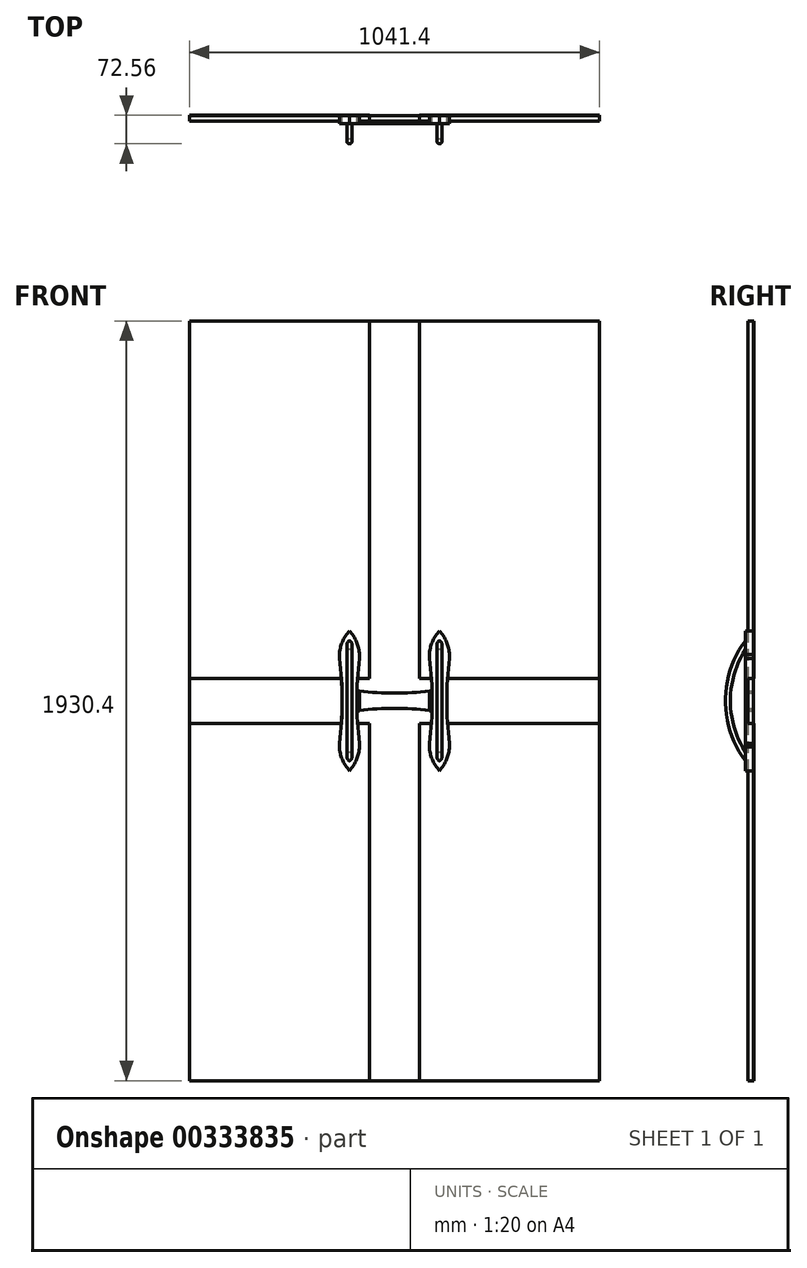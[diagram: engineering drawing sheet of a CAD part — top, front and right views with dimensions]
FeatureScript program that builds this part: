
annotation { "Feature Type Name" : "Feature", "Feature Type Description" : "" }
export const myFeature = defineFeature(function(context is Context, id is Id, definition is map)
    precondition{}
    {
        {
            var Q0;
            Q0=qCreatedBy(makeId("Front.planeOp"),FACE);
            var sketch = newSketch(context, id + "F0", { "sketchPlane" : qUnion([Q0])});
            skLineSegment(sketch, "E0.bottom", {"start": v(-936, -960.25) * mm, "end": v(105.4, -960.25) * mm});
            skLineSegment(sketch, "E0.top", {"start": v(-936, 970.15) * mm, "end": v(105.4, 970.15) * mm});
            skLineSegment(sketch, "E0.left", {"start": v(-936, -960.25) * mm, "end": v(-936, 970.15) * mm});
            skLineSegment(sketch, "E0.right", {"start": v(105.4, -960.25) * mm, "end": v(105.4, 970.15) * mm});
            skLineSegment(sketch, "E1", {"start": v(-478.8, 970.15) * mm, "end": v(-478.8, 62.1) * mm});
            skLineSegment(sketch, "E2", {"start": v(-478.8, 62.1) * mm, "end": v(-936, 62.1) * mm});
            skLineSegment(sketch, "E3", {"start": v(-351.8, 970.15) * mm, "end": v(-351.8, 62.1) * mm});
            skLineSegment(sketch, "E4", {"start": v(-351.8, 62.1) * mm, "end": v(105.4, 62.1) * mm});
            skLineSegment(sketch, "E5", {"start": v(105.4, -52.2) * mm, "end": v(-351.8, -52.2) * mm});
            skLineSegment(sketch, "E6", {"start": v(-351.8, -52.2) * mm, "end": v(-351.8, -960.25) * mm});
            skLineSegment(sketch, "E7", {"start": v(-936, -52.2) * mm, "end": v(-478.8, -52.2) * mm});
            skLineSegment(sketch, "E8", {"start": v(-478.8, -52.2) * mm, "end": v(-478.8, -960.25) * mm});
            skLineSegment(sketch, "E9", {"start": v(-415.3, 970.15) * mm, "end": v(-415.3, -960.25) * mm});
            skLineSegment(sketch, "E10.bottom", {"start": v(-555, 182.75) * mm, "end": v(-504.2, 182.75) * mm});
            skLineSegment(sketch, "E10.top", {"start": v(-555, -172.85) * mm, "end": v(-504.2, -172.85) * mm});
            skLineSegment(sketch, "E10.left", {"start": v(-555, 182.75) * mm, "end": v(-555, -172.85) * mm});
            skLineSegment(sketch, "E10.right", {"start": v(-504.2, 182.75) * mm, "end": v(-504.2, -172.85) * mm});
            skLineSegment(sketch, "E11.bottom", {"start": v(-326.4, 182.75) * mm, "end": v(-275.6, 182.75) * mm});
            skLineSegment(sketch, "E11.top", {"start": v(-326.4, -172.85) * mm, "end": v(-275.6, -172.85) * mm});
            skLineSegment(sketch, "E11.left", {"start": v(-326.4, 182.75) * mm, "end": v(-326.4, -172.85) * mm});
            skLineSegment(sketch, "E11.right", {"start": v(-275.6, 182.75) * mm, "end": v(-275.6, -172.85) * mm});
            skLineSegment(sketch, "E12.bottom", {"start": v(-510.66, 30.35) * mm, "end": v(-319.94, 30.35) * mm});
            skLineSegment(sketch, "E12.top", {"start": v(-510.66, -20.45) * mm, "end": v(-319.94, -20.45) * mm});
            skLineSegment(sketch, "E12.left", {"start": v(-504.2, 30.35) * mm, "end": v(-504.2, -20.45) * mm});
            skLineSegment(sketch, "E12.right", {"start": v(-326.4, 30.35) * mm, "end": v(-326.4, -20.45) * mm});
            skArc(sketch, "E13", {"start": v(-555, -103.11) * mm, "mid": v(-549.29, -140.52) * mm, "end": v(-529.6, -172.85) * mm});
            skLineSegment(sketch, "E14", {"start": v(-936, 4.95) * mm, "end": v(105.4, 4.95) * mm});
            skArc(sketch, "E15.MirrorCS", {"start": v(-555, 113.02) * mm, "mid": v(-549.29, 150.43) * mm, "end": v(-529.6, 182.75) * mm});
            skArc(sketch, "E16.MirrorCS", {"start": v(-275.6, -103.11) * mm, "mid": v(-281.31, -140.52) * mm, "end": v(-301, -172.85) * mm});
            skArc(sketch, "E17.MirrorCS", {"start": v(-275.6, 113.02) * mm, "mid": v(-281.31, 150.43) * mm, "end": v(-301, 182.75) * mm});
            skLineSegment(sketch, "E18", {"start": v(-529.6, -172.85) * mm, "end": v(-529.6, -92.29) * mm});
            skArc(sketch, "E19.MirrorCS", {"start": v(-504.2, -103.11) * mm, "mid": v(-509.91, -140.52) * mm, "end": v(-529.6, -172.85) * mm});
            skArc(sketch, "E20.MirrorCS", {"start": v(-504.2, 113.02) * mm, "mid": v(-509.91, 150.43) * mm, "end": v(-529.6, 182.75) * mm});
            skArc(sketch, "E21.MirrorCS", {"start": v(-326.4, 113.02) * mm, "mid": v(-320.69, 150.43) * mm, "end": v(-301, 182.75) * mm});
            skArc(sketch, "E22.MirrorCS", {"start": v(-326.4, -103.11) * mm, "mid": v(-320.69, -140.52) * mm, "end": v(-301, -172.85) * mm});
            skArc(sketch, "E23", {"start": v(-555, -103.11) * mm, "mid": v(-548.16, 4.95) * mm, "end": v(-555, 113.02) * mm});
            skArc(sketch, "E24.MirrorCS", {"start": v(-504.2, -103.11) * mm, "mid": v(-511.03, 4.95) * mm, "end": v(-504.2, 113.02) * mm});
            skArc(sketch, "E25.MirrorCS", {"start": v(-275.6, -103.11) * mm, "mid": v(-282.43, 4.95) * mm, "end": v(-275.6, 113.02) * mm});
            skArc(sketch, "E26.MirrorCS", {"start": v(-326.4, -103.11) * mm, "mid": v(-319.56, 4.95) * mm, "end": v(-326.4, 113.02) * mm});
            skArc(sketch, "E27", {"start": v(-319.94, -20.45) * mm, "mid": v(-415.3, -14.24) * mm, "end": v(-510.66, -20.45) * mm});
            skArc(sketch, "E28.MirrorCS", {"start": v(-319.94, 30.35) * mm, "mid": v(-415.3, 24.14) * mm, "end": v(-510.66, 30.35) * mm});
            skSolve(sketch);
        }
        {
            var Q0;
            {var subQ9=sQuery(id+"F0.wireOp",EDGE,"E3");Q0=makeQuery(id+"F0.imprint","IMPRINT",FACE,{"disambiguationData":[TD([[makeQuery(id+"F0.imprint","IMPRINT",EDGE,{"derivedFrom":subQ9}),-1.0]])]});}
            var Q1;
            {var subQ1=sQuery(id+"F0.wireOp",EDGE,"E1");Q1=makeQuery(id+"F0.imprint","IMPRINT",FACE,{"disambiguationData":[TD([[makeQuery(id+"F0.imprint","IMPRINT",EDGE,{"derivedFrom":subQ1}),1.0]])]});}
            var Q2;
            {var subQ0=sQuery(id+"F0.wireOp",EDGE,"E4");var subQ1=sQuery(id+"F0.wireOp",EDGE,"E0.right");var subQ2=makeQuery(id+"F0.imprint","INTERSECT",VERTEX,{"derivedFrom":[subQ1,subQ0]});Q2=makeQuery(id+"F0.imprint","IMPRINT",FACE,{"disambiguationData":[TD([[makeQuery(id+"F0.imprint","IMPRINT",EDGE,{"disambiguationData":[TD([[subQ2,1.0]])],"derivedFrom":subQ1}),1.0]])]});}
            var Q3;
            {var subQ0=sQuery(id+"F0.wireOp",EDGE,"E5");var subQ1=sQuery(id+"F0.wireOp",EDGE,"E0.right");var subQ2=makeQuery(id+"F0.imprint","INTERSECT",VERTEX,{"derivedFrom":[subQ1,subQ0]});Q3=makeQuery(id+"F0.imprint","IMPRINT",FACE,{"disambiguationData":[TD([[makeQuery(id+"F0.imprint","IMPRINT",EDGE,{"disambiguationData":[TD([[subQ2,-1.0]])],"derivedFrom":subQ1}),1.0]])]});}
            var Q4;
            {var subQ5=sQuery(id+"F0.wireOp",EDGE,"E6");Q4=makeQuery(id+"F0.imprint","IMPRINT",FACE,{"disambiguationData":[TD([[makeQuery(id+"F0.imprint","IMPRINT",EDGE,{"derivedFrom":subQ5}),-1.0]])]});}
            var Q5;
            {var subQ5=sQuery(id+"F0.wireOp",EDGE,"E8");Q5=makeQuery(id+"F0.imprint","IMPRINT",FACE,{"disambiguationData":[TD([[makeQuery(id+"F0.imprint","IMPRINT",EDGE,{"derivedFrom":subQ5}),1.0]])]});}
            var Q6;
            {var subQ0=sQuery(id+"F0.wireOp",EDGE,"E7");var subQ1=sQuery(id+"F0.wireOp",EDGE,"E0.left");var subQ2=makeQuery(id+"F0.imprint","INTERSECT",VERTEX,{"derivedFrom":[subQ1,subQ0]});Q6=makeQuery(id+"F0.imprint","IMPRINT",FACE,{"disambiguationData":[TD([[makeQuery(id+"F0.imprint","IMPRINT",EDGE,{"disambiguationData":[TD([[subQ2,-1.0]])],"derivedFrom":subQ1}),-1.0]])]});}
            var Q7;
            {var subQ0=sQuery(id+"F0.wireOp",EDGE,"E2");var subQ1=sQuery(id+"F0.wireOp",EDGE,"E0.left");var subQ2=makeQuery(id+"F0.imprint","INTERSECT",VERTEX,{"derivedFrom":[subQ1,subQ0]});Q7=makeQuery(id+"F0.imprint","IMPRINT",FACE,{"disambiguationData":[TD([[makeQuery(id+"F0.imprint","IMPRINT",EDGE,{"disambiguationData":[TD([[subQ2,1.0]])],"derivedFrom":subQ1}),-1.0]])]});}
            var Q8;
            {var subQ0=sQuery(id+"F0.wireOp",EDGE,"E24.MirrorCS");var subQ1=sQuery(id+"F0.wireOp",EDGE,"E7");var subQ2=makeQuery(id+"F0.imprint","INTERSECT",VERTEX,{"derivedFrom":[subQ1,subQ0]});Q8=makeQuery(id+"F0.imprint","IMPRINT",FACE,{"disambiguationData":[TD([[makeQuery(id+"F0.imprint","IMPRINT",EDGE,{"disambiguationData":[TD([[subQ2,-1.0]])],"derivedFrom":subQ1}),1.0]])]});}
            var Q9;
            {var subQ0=sQuery(id+"F0.wireOp",EDGE,"E10.left");var subQ1=sQuery(id+"F0.wireOp",EDGE,"E7");var subQ2=makeQuery(id+"F0.imprint","INTERSECT",VERTEX,{"derivedFrom":[subQ1,subQ0]});Q9=makeQuery(id+"F0.imprint","IMPRINT",FACE,{"disambiguationData":[TD([[makeQuery(id+"F0.imprint","IMPRINT",EDGE,{"disambiguationData":[TD([[subQ2,-1.0]])],"derivedFrom":subQ1}),1.0]])]});}
            var Q10;
            {var subQ0=sQuery(id+"F0.wireOp",EDGE,"E23");var subQ1=sQuery(id+"F0.wireOp",EDGE,"E2");var subQ2=makeQuery(id+"F0.imprint","INTERSECT",VERTEX,{"derivedFrom":[subQ1,subQ0]});Q10=makeQuery(id+"F0.imprint","IMPRINT",FACE,{"disambiguationData":[TD([[makeQuery(id+"F0.imprint","IMPRINT",EDGE,{"disambiguationData":[TD([[subQ2,-1.0]])],"derivedFrom":subQ1}),1.0]])]});}
            var Q11;
            {var subQ0=sQuery(id+"F0.wireOp",EDGE,"E10.right");var subQ1=sQuery(id+"F0.wireOp",EDGE,"E2");var subQ2=makeQuery(id+"F0.imprint","INTERSECT",VERTEX,{"derivedFrom":[subQ1,subQ0]});Q11=makeQuery(id+"F0.imprint","IMPRINT",FACE,{"disambiguationData":[TD([[makeQuery(id+"F0.imprint","IMPRINT",EDGE,{"disambiguationData":[TD([[subQ2,-1.0]])],"derivedFrom":subQ1}),1.0]])]});}
            var Q12;
            {var subQ0=sQuery(id+"F0.wireOp",EDGE,"E11.left");var subQ1=sQuery(id+"F0.wireOp",EDGE,"E4");var subQ2=makeQuery(id+"F0.imprint","INTERSECT",VERTEX,{"derivedFrom":[subQ1,subQ0]});Q12=makeQuery(id+"F0.imprint","IMPRINT",FACE,{"disambiguationData":[TD([[makeQuery(id+"F0.imprint","IMPRINT",EDGE,{"disambiguationData":[TD([[subQ2,-1.0]])],"derivedFrom":subQ1}),-1.0]])]});}
            var Q13;
            {var subQ0=sQuery(id+"F0.wireOp",EDGE,"E26.MirrorCS");var subQ1=sQuery(id+"F0.wireOp",EDGE,"E5");var subQ2=makeQuery(id+"F0.imprint","INTERSECT",VERTEX,{"derivedFrom":[subQ1,subQ0]});Q13=makeQuery(id+"F0.imprint","IMPRINT",FACE,{"disambiguationData":[TD([[makeQuery(id+"F0.imprint","IMPRINT",EDGE,{"disambiguationData":[TD([[subQ2,-1.0]])],"derivedFrom":subQ1}),-1.0]])]});}
            var Q14;
            {var subQ0=sQuery(id+"F0.wireOp",EDGE,"E27");var subQ1=sQuery(id+"F0.wireOp",EDGE,"E9");var subQ2=makeQuery(id+"F0.imprint","INTERSECT",VERTEX,{"derivedFrom":[subQ1,subQ0]});Q14=makeQuery(id+"F0.imprint","IMPRINT",FACE,{"disambiguationData":[TD([[makeQuery(id+"F0.imprint","IMPRINT",EDGE,{"disambiguationData":[TD([[subQ2,-1.0]])],"derivedFrom":subQ1}),1.0]])]});}
            var Q15;
            {var subQ0=sQuery(id+"F0.wireOp",EDGE,"E27");var subQ1=sQuery(id+"F0.wireOp",EDGE,"E9");var subQ2=makeQuery(id+"F0.imprint","INTERSECT",VERTEX,{"derivedFrom":[subQ1,subQ0]});Q15=makeQuery(id+"F0.imprint","IMPRINT",FACE,{"disambiguationData":[TD([[makeQuery(id+"F0.imprint","IMPRINT",EDGE,{"disambiguationData":[TD([[subQ2,-1.0]])],"derivedFrom":subQ1}),-1.0]])]});}
            var Q16;
            {var subQ0=sQuery(id+"F0.wireOp",EDGE,"E12.bottom");var subQ1=sQuery(id+"F0.wireOp",EDGE,"E9");var subQ2=makeQuery(id+"F0.imprint","INTERSECT",VERTEX,{"derivedFrom":[subQ1,subQ0]});Q16=makeQuery(id+"F0.imprint","IMPRINT",FACE,{"disambiguationData":[TD([[makeQuery(id+"F0.imprint","IMPRINT",EDGE,{"disambiguationData":[TD([[subQ2,-1.0]])],"derivedFrom":subQ1}),-1.0]])]});}
            var Q17;
            {var subQ0=sQuery(id+"F0.wireOp",EDGE,"E12.bottom");var subQ1=sQuery(id+"F0.wireOp",EDGE,"E9");var subQ2=makeQuery(id+"F0.imprint","INTERSECT",VERTEX,{"derivedFrom":[subQ1,subQ0]});Q17=makeQuery(id+"F0.imprint","IMPRINT",FACE,{"disambiguationData":[TD([[makeQuery(id+"F0.imprint","IMPRINT",EDGE,{"disambiguationData":[TD([[subQ2,-1.0]])],"derivedFrom":subQ1}),1.0]])]});}
            var Q18;
            {var subQ0=sQuery(id+"F0.wireOp",EDGE,"E11.right");var subQ1=sQuery(id+"F0.wireOp",EDGE,"E5");var subQ2=makeQuery(id+"F0.imprint","INTERSECT",VERTEX,{"derivedFrom":[subQ1,subQ0]});Q18=makeQuery(id+"F0.imprint","IMPRINT",FACE,{"disambiguationData":[TD([[makeQuery(id+"F0.imprint","IMPRINT",EDGE,{"disambiguationData":[TD([[subQ2,-1.0]])],"derivedFrom":subQ1}),-1.0]])]});}
            var Q19;
            {var subQ0=sQuery(id+"F0.wireOp",EDGE,"E25.MirrorCS");var subQ1=sQuery(id+"F0.wireOp",EDGE,"E4");var subQ2=makeQuery(id+"F0.imprint","INTERSECT",VERTEX,{"derivedFrom":[subQ1,subQ0]});Q19=makeQuery(id+"F0.imprint","IMPRINT",FACE,{"disambiguationData":[TD([[makeQuery(id+"F0.imprint","IMPRINT",EDGE,{"disambiguationData":[TD([[subQ2,-1.0]])],"derivedFrom":subQ1}),-1.0]])]});}
            extrude(context, id + "F1", {"entities" : qUnion([Q0, Q1, Q2, Q3, Q4, Q5, Q6, Q7, Q8, Q9, Q10, Q11, Q12, Q13, Q14, Q15, Q16, Q17, Q18, Q19]), "depth" : 14.29 * mm});
        }
        {
            var Q0;
            {var subQ14=sQuery(id+"F0.wireOp",EDGE,"E3");Q0=makeQuery(id+"F0.imprint","IMPRINT",FACE,{"disambiguationData":[TD([[makeQuery(id+"F0.imprint","IMPRINT",EDGE,{"derivedFrom":subQ14}),1.0]])]});}
            var Q1;
            {var subQ16=sQuery(id+"F0.wireOp",EDGE,"E1");Q1=makeQuery(id+"F0.imprint","IMPRINT",FACE,{"disambiguationData":[TD([[makeQuery(id+"F0.imprint","IMPRINT",EDGE,{"derivedFrom":subQ16}),-1.0]])]});}
            var Q2;
            {var subQ11=sQuery(id+"F0.wireOp",EDGE,"E8");Q2=makeQuery(id+"F0.imprint","IMPRINT",FACE,{"disambiguationData":[TD([[makeQuery(id+"F0.imprint","IMPRINT",EDGE,{"derivedFrom":subQ11}),-1.0]])]});}
            var Q3;
            {var subQ10=sQuery(id+"F0.wireOp",EDGE,"E6");Q3=makeQuery(id+"F0.imprint","IMPRINT",FACE,{"disambiguationData":[TD([[makeQuery(id+"F0.imprint","IMPRINT",EDGE,{"derivedFrom":subQ10}),1.0]])]});}
            var Q4;
            {var subQ0=sQuery(id+"F0.wireOp",EDGE,"E11.right");var subQ1=sQuery(id+"F0.wireOp",EDGE,"E11.bottom");var subQ2=makeQuery(id+"F0.imprint","INTERSECT",VERTEX,{"derivedFrom":[subQ1,subQ0]});Q4=makeQuery(id+"F0.imprint","IMPRINT",FACE,{"disambiguationData":[TD([[makeQuery(id+"F0.imprint","IMPRINT",EDGE,{"disambiguationData":[TD([[subQ2,-1.0]])],"derivedFrom":subQ0}),-1.0]])]});}
            var Q5;
            {var subQ0=sQuery(id+"F0.wireOp",EDGE,"E11.left");var subQ1=sQuery(id+"F0.wireOp",EDGE,"E11.bottom");var subQ2=makeQuery(id+"F0.imprint","INTERSECT",VERTEX,{"derivedFrom":[subQ1,subQ0]});Q5=makeQuery(id+"F0.imprint","IMPRINT",FACE,{"disambiguationData":[TD([[makeQuery(id+"F0.imprint","IMPRINT",EDGE,{"disambiguationData":[TD([[subQ2,-1.0]])],"derivedFrom":subQ0}),1.0]])]});}
            var Q6;
            {var subQ0=sQuery(id+"F0.wireOp",EDGE,"E10.right");var subQ1=sQuery(id+"F0.wireOp",EDGE,"E10.bottom");var subQ2=makeQuery(id+"F0.imprint","INTERSECT",VERTEX,{"derivedFrom":[subQ1,subQ0]});Q6=makeQuery(id+"F0.imprint","IMPRINT",FACE,{"disambiguationData":[TD([[makeQuery(id+"F0.imprint","IMPRINT",EDGE,{"disambiguationData":[TD([[subQ2,-1.0]])],"derivedFrom":subQ0}),-1.0]])]});}
            var Q7;
            {var subQ0=sQuery(id+"F0.wireOp",EDGE,"E10.left");var subQ1=sQuery(id+"F0.wireOp",EDGE,"E10.bottom");var subQ2=makeQuery(id+"F0.imprint","INTERSECT",VERTEX,{"derivedFrom":[subQ1,subQ0]});Q7=makeQuery(id+"F0.imprint","IMPRINT",FACE,{"disambiguationData":[TD([[makeQuery(id+"F0.imprint","IMPRINT",EDGE,{"disambiguationData":[TD([[subQ2,-1.0]])],"derivedFrom":subQ0}),1.0]])]});}
            var Q8;
            {var subQ0=sQuery(id+"F0.wireOp",EDGE,"E10.left");var subQ1=sQuery(id+"F0.wireOp",EDGE,"E10.top");var subQ2=makeQuery(id+"F0.imprint","INTERSECT",VERTEX,{"derivedFrom":[subQ1,subQ0]});Q8=makeQuery(id+"F0.imprint","IMPRINT",FACE,{"disambiguationData":[TD([[makeQuery(id+"F0.imprint","IMPRINT",EDGE,{"disambiguationData":[TD([[subQ2,1.0]])],"derivedFrom":subQ0}),1.0]])]});}
            var Q9;
            {var subQ0=sQuery(id+"F0.wireOp",EDGE,"E10.right");var subQ1=sQuery(id+"F0.wireOp",EDGE,"E10.top");var subQ2=makeQuery(id+"F0.imprint","INTERSECT",VERTEX,{"derivedFrom":[subQ1,subQ0]});Q9=makeQuery(id+"F0.imprint","IMPRINT",FACE,{"disambiguationData":[TD([[makeQuery(id+"F0.imprint","IMPRINT",EDGE,{"disambiguationData":[TD([[subQ2,1.0]])],"derivedFrom":subQ0}),-1.0]])]});}
            var Q10;
            {var subQ0=sQuery(id+"F0.wireOp",EDGE,"E11.left");var subQ1=sQuery(id+"F0.wireOp",EDGE,"E11.top");var subQ2=makeQuery(id+"F0.imprint","INTERSECT",VERTEX,{"derivedFrom":[subQ1,subQ0]});Q10=makeQuery(id+"F0.imprint","IMPRINT",FACE,{"disambiguationData":[TD([[makeQuery(id+"F0.imprint","IMPRINT",EDGE,{"disambiguationData":[TD([[subQ2,1.0]])],"derivedFrom":subQ0}),1.0]])]});}
            var Q11;
            {var subQ0=sQuery(id+"F0.wireOp",EDGE,"E11.right");var subQ1=sQuery(id+"F0.wireOp",EDGE,"E11.top");var subQ2=makeQuery(id+"F0.imprint","INTERSECT",VERTEX,{"derivedFrom":[subQ1,subQ0]});Q11=makeQuery(id+"F0.imprint","IMPRINT",FACE,{"disambiguationData":[TD([[makeQuery(id+"F0.imprint","IMPRINT",EDGE,{"disambiguationData":[TD([[subQ2,1.0]])],"derivedFrom":subQ0}),-1.0]])]});}
            var Q12;
            {var subQ0=sQuery(id+"F0.wireOp",EDGE,"E23");var subQ1=sQuery(id+"F0.wireOp",EDGE,"E2");var subQ2=makeQuery(id+"F0.imprint","INTERSECT",VERTEX,{"derivedFrom":[subQ1,subQ0]});Q12=makeQuery(id+"F0.imprint","IMPRINT",FACE,{"disambiguationData":[TD([[makeQuery(id+"F0.imprint","IMPRINT",EDGE,{"disambiguationData":[TD([[subQ2,-1.0]])],"derivedFrom":subQ1}),-1.0]])]});}
            var Q13;
            {var subQ0=sQuery(id+"F0.wireOp",EDGE,"E10.right");var subQ1=sQuery(id+"F0.wireOp",EDGE,"E2");var subQ2=makeQuery(id+"F0.imprint","INTERSECT",VERTEX,{"derivedFrom":[subQ1,subQ0]});Q13=makeQuery(id+"F0.imprint","IMPRINT",FACE,{"disambiguationData":[TD([[makeQuery(id+"F0.imprint","IMPRINT",EDGE,{"disambiguationData":[TD([[subQ2,-1.0]])],"derivedFrom":subQ1}),-1.0]])]});}
            var Q14;
            {var subQ0=sQuery(id+"F0.wireOp",EDGE,"E24.MirrorCS");var subQ1=sQuery(id+"F0.wireOp",EDGE,"E7");var subQ2=makeQuery(id+"F0.imprint","INTERSECT",VERTEX,{"derivedFrom":[subQ1,subQ0]});Q14=makeQuery(id+"F0.imprint","IMPRINT",FACE,{"disambiguationData":[TD([[makeQuery(id+"F0.imprint","IMPRINT",EDGE,{"disambiguationData":[TD([[subQ2,-1.0]])],"derivedFrom":subQ1}),-1.0]])]});}
            var Q15;
            {var subQ0=sQuery(id+"F0.wireOp",EDGE,"E10.left");var subQ1=sQuery(id+"F0.wireOp",EDGE,"E7");var subQ2=makeQuery(id+"F0.imprint","INTERSECT",VERTEX,{"derivedFrom":[subQ1,subQ0]});Q15=makeQuery(id+"F0.imprint","IMPRINT",FACE,{"disambiguationData":[TD([[makeQuery(id+"F0.imprint","IMPRINT",EDGE,{"disambiguationData":[TD([[subQ2,-1.0]])],"derivedFrom":subQ1}),-1.0]])]});}
            var Q16;
            {var subQ0=sQuery(id+"F0.wireOp",EDGE,"E11.right");var subQ1=sQuery(id+"F0.wireOp",EDGE,"E5");var subQ2=makeQuery(id+"F0.imprint","INTERSECT",VERTEX,{"derivedFrom":[subQ1,subQ0]});Q16=makeQuery(id+"F0.imprint","IMPRINT",FACE,{"disambiguationData":[TD([[makeQuery(id+"F0.imprint","IMPRINT",EDGE,{"disambiguationData":[TD([[subQ2,-1.0]])],"derivedFrom":subQ1}),1.0]])]});}
            var Q17;
            {var subQ0=sQuery(id+"F0.wireOp",EDGE,"E26.MirrorCS");var subQ1=sQuery(id+"F0.wireOp",EDGE,"E5");var subQ2=makeQuery(id+"F0.imprint","INTERSECT",VERTEX,{"derivedFrom":[subQ1,subQ0]});Q17=makeQuery(id+"F0.imprint","IMPRINT",FACE,{"disambiguationData":[TD([[makeQuery(id+"F0.imprint","IMPRINT",EDGE,{"disambiguationData":[TD([[subQ2,-1.0]])],"derivedFrom":subQ1}),1.0]])]});}
            var Q18;
            {var subQ0=sQuery(id+"F0.wireOp",EDGE,"E11.left");var subQ1=sQuery(id+"F0.wireOp",EDGE,"E4");var subQ2=makeQuery(id+"F0.imprint","INTERSECT",VERTEX,{"derivedFrom":[subQ1,subQ0]});Q18=makeQuery(id+"F0.imprint","IMPRINT",FACE,{"disambiguationData":[TD([[makeQuery(id+"F0.imprint","IMPRINT",EDGE,{"disambiguationData":[TD([[subQ2,-1.0]])],"derivedFrom":subQ1}),1.0]])]});}
            var Q19;
            {var subQ0=sQuery(id+"F0.wireOp",EDGE,"E25.MirrorCS");var subQ1=sQuery(id+"F0.wireOp",EDGE,"E4");var subQ2=makeQuery(id+"F0.imprint","INTERSECT",VERTEX,{"derivedFrom":[subQ1,subQ0]});Q19=makeQuery(id+"F0.imprint","IMPRINT",FACE,{"disambiguationData":[TD([[makeQuery(id+"F0.imprint","IMPRINT",EDGE,{"disambiguationData":[TD([[subQ2,-1.0]])],"derivedFrom":subQ1}),1.0]])]});}
            extrude(context, id + "F2", {"entities" : qUnion([Q0, Q1, Q2, Q3, Q4, Q5, Q6, Q7, Q8, Q9, Q10, Q11, Q12, Q13, Q14, Q15, Q16, Q17, Q18, Q19]), "oppositeDirection" : true, "depth" : ((1 + 11 / 16) - 9 / 16) * mm});
        }
        {
            var Q0;
            {var subQ5=sQuery(id+"F0.wireOp",EDGE,"E24.MirrorCS");var subQ8=sQuery(id+"F0.wireOp",EDGE,"E2");var subQ9=makeQuery(id+"F0.imprint","INTERSECT",VERTEX,{"derivedFrom":[subQ8,subQ5]});Q0=makeQuery(id+"F0.imprint","IMPRINT",FACE,{"disambiguationData":[TD([[makeQuery(id+"F0.imprint","IMPRINT",EDGE,{"disambiguationData":[TD([[subQ9,-1.0]])],"derivedFrom":subQ8}),-1.0]])]});}
            var Q1;
            {var subQ0=sQuery(id+"F0.wireOp",EDGE,"E24.MirrorCS");var subQ5=sQuery(id+"F0.wireOp",EDGE,"E2");var subQ8=makeQuery(id+"F0.imprint","INTERSECT",VERTEX,{"derivedFrom":[subQ5,subQ0]});Q1=makeQuery(id+"F0.imprint","IMPRINT",FACE,{"disambiguationData":[TD([[makeQuery(id+"F0.imprint","IMPRINT",EDGE,{"disambiguationData":[TD([[subQ8,-1.0]])],"derivedFrom":subQ5}),1.0]])]});}
            var Q2;
            {var subQ2=sQuery(id+"F0.wireOp",EDGE,"E7");var subQ4=sQuery(id+"F0.wireOp",EDGE,"E23");var subQ5=makeQuery(id+"F0.imprint","INTERSECT",VERTEX,{"derivedFrom":[subQ2,subQ4]});Q2=makeQuery(id+"F0.imprint","IMPRINT",FACE,{"disambiguationData":[TD([[makeQuery(id+"F0.imprint","IMPRINT",EDGE,{"disambiguationData":[TD([[subQ5,-1.0]])],"derivedFrom":subQ2}),1.0]])]});}
            var Q3;
            {var subQ9=sQuery(id+"F0.wireOp",EDGE,"E23");var subQ11=sQuery(id+"F0.wireOp",EDGE,"E7");var subQ12=makeQuery(id+"F0.imprint","INTERSECT",VERTEX,{"derivedFrom":[subQ11,subQ9]});Q3=makeQuery(id+"F0.imprint","IMPRINT",FACE,{"disambiguationData":[TD([[makeQuery(id+"F0.imprint","IMPRINT",EDGE,{"disambiguationData":[TD([[subQ12,-1.0]])],"derivedFrom":subQ11}),-1.0]])]});}
            var Q4;
            {var subQ0=sQuery(id+"F0.wireOp",EDGE,"E14");var subQ1=sQuery(id+"F0.wireOp",EDGE,"E9");var subQ2=makeQuery(id+"F0.imprint","INTERSECT",VERTEX,{"derivedFrom":[subQ1,subQ0]});Q4=makeQuery(id+"F0.imprint","IMPRINT",FACE,{"disambiguationData":[TD([[makeQuery(id+"F0.imprint","IMPRINT",EDGE,{"disambiguationData":[TD([[subQ2,-1.0]])],"derivedFrom":subQ1}),-1.0]])]});}
            var Q5;
            {var subQ0=sQuery(id+"F0.wireOp",EDGE,"E28.MirrorCS");var subQ1=sQuery(id+"F0.wireOp",EDGE,"E9");var subQ2=makeQuery(id+"F0.imprint","INTERSECT",VERTEX,{"derivedFrom":[subQ1,subQ0]});Q5=makeQuery(id+"F0.imprint","IMPRINT",FACE,{"disambiguationData":[TD([[makeQuery(id+"F0.imprint","IMPRINT",EDGE,{"disambiguationData":[TD([[subQ2,-1.0]])],"derivedFrom":subQ1}),-1.0]])]});}
            var Q6;
            {var subQ0=sQuery(id+"F0.wireOp",EDGE,"E28.MirrorCS");var subQ1=sQuery(id+"F0.wireOp",EDGE,"E9");var subQ2=makeQuery(id+"F0.imprint","INTERSECT",VERTEX,{"derivedFrom":[subQ1,subQ0]});Q6=makeQuery(id+"F0.imprint","IMPRINT",FACE,{"disambiguationData":[TD([[makeQuery(id+"F0.imprint","IMPRINT",EDGE,{"disambiguationData":[TD([[subQ2,-1.0]])],"derivedFrom":subQ1}),1.0]])]});}
            var Q7;
            {var subQ0=sQuery(id+"F0.wireOp",EDGE,"E14");var subQ1=sQuery(id+"F0.wireOp",EDGE,"E9");var subQ2=makeQuery(id+"F0.imprint","INTERSECT",VERTEX,{"derivedFrom":[subQ1,subQ0]});Q7=makeQuery(id+"F0.imprint","IMPRINT",FACE,{"disambiguationData":[TD([[makeQuery(id+"F0.imprint","IMPRINT",EDGE,{"disambiguationData":[TD([[subQ2,-1.0]])],"derivedFrom":subQ1}),1.0]])]});}
            var Q8;
            {var subQ2=sQuery(id+"F0.wireOp",EDGE,"E5");var subQ4=sQuery(id+"F0.wireOp",EDGE,"E25.MirrorCS");var subQ5=makeQuery(id+"F0.imprint","INTERSECT",VERTEX,{"derivedFrom":[subQ2,subQ4]});Q8=makeQuery(id+"F0.imprint","IMPRINT",FACE,{"disambiguationData":[TD([[makeQuery(id+"F0.imprint","IMPRINT",EDGE,{"disambiguationData":[TD([[subQ5,-1.0]])],"derivedFrom":subQ2}),-1.0]])]});}
            var Q9;
            {var subQ0=sQuery(id+"F0.wireOp",EDGE,"E26.MirrorCS");var subQ6=sQuery(id+"F0.wireOp",EDGE,"E4");var subQ8=makeQuery(id+"F0.imprint","INTERSECT",VERTEX,{"derivedFrom":[subQ6,subQ0]});Q9=makeQuery(id+"F0.imprint","IMPRINT",FACE,{"disambiguationData":[TD([[makeQuery(id+"F0.imprint","IMPRINT",EDGE,{"disambiguationData":[TD([[subQ8,-1.0]])],"derivedFrom":subQ6}),-1.0]])]});}
            var Q10;
            {var subQ7=sQuery(id+"F0.wireOp",EDGE,"E4");var subQ9=sQuery(id+"F0.wireOp",EDGE,"E26.MirrorCS");var subQ13=makeQuery(id+"F0.imprint","INTERSECT",VERTEX,{"derivedFrom":[subQ7,subQ9]});Q10=makeQuery(id+"F0.imprint","IMPRINT",FACE,{"disambiguationData":[TD([[makeQuery(id+"F0.imprint","IMPRINT",EDGE,{"disambiguationData":[TD([[subQ13,-1.0]])],"derivedFrom":subQ7}),1.0]])]});}
            var Q11;
            {var subQ5=sQuery(id+"F0.wireOp",EDGE,"E25.MirrorCS");var subQ11=sQuery(id+"F0.wireOp",EDGE,"E5");var subQ13=makeQuery(id+"F0.imprint","INTERSECT",VERTEX,{"derivedFrom":[subQ11,subQ5]});Q11=makeQuery(id+"F0.imprint","IMPRINT",FACE,{"disambiguationData":[TD([[makeQuery(id+"F0.imprint","IMPRINT",EDGE,{"disambiguationData":[TD([[subQ13,-1.0]])],"derivedFrom":subQ11}),1.0]])]});}
            var Q12;
            {var subQ0=sQuery(id+"F0.wireOp",EDGE,"E14");var subQ1=sQuery(id+"F0.wireOp",EDGE,"E12.right");var subQ2=makeQuery(id+"F0.imprint","INTERSECT",VERTEX,{"derivedFrom":[subQ1,subQ0]});Q12=makeQuery(id+"F0.imprint","IMPRINT",FACE,{"disambiguationData":[TD([[makeQuery(id+"F0.imprint","IMPRINT",EDGE,{"disambiguationData":[TD([[subQ2,-1.0]])],"derivedFrom":subQ1}),1.0]])]});}
            var Q13;
            {var subQ0=sQuery(id+"F0.wireOp",EDGE,"E28.MirrorCS");var subQ1=sQuery(id+"F0.wireOp",EDGE,"E12.right");var subQ2=makeQuery(id+"F0.imprint","INTERSECT",VERTEX,{"derivedFrom":[subQ1,subQ0]});Q13=makeQuery(id+"F0.imprint","IMPRINT",FACE,{"disambiguationData":[TD([[makeQuery(id+"F0.imprint","IMPRINT",EDGE,{"disambiguationData":[TD([[subQ2,-1.0]])],"derivedFrom":subQ1}),1.0]])]});}
            var Q14;
            {var subQ0=sQuery(id+"F0.wireOp",EDGE,"E28.MirrorCS");var subQ1=sQuery(id+"F0.wireOp",EDGE,"E12.left");var subQ2=makeQuery(id+"F0.imprint","INTERSECT",VERTEX,{"derivedFrom":[subQ1,subQ0]});Q14=makeQuery(id+"F0.imprint","IMPRINT",FACE,{"disambiguationData":[TD([[makeQuery(id+"F0.imprint","IMPRINT",EDGE,{"disambiguationData":[TD([[subQ2,-1.0]])],"derivedFrom":subQ1}),-1.0]])]});}
            var Q15;
            {var subQ0=sQuery(id+"F0.wireOp",EDGE,"E14");var subQ1=sQuery(id+"F0.wireOp",EDGE,"E12.left");var subQ2=makeQuery(id+"F0.imprint","INTERSECT",VERTEX,{"derivedFrom":[subQ1,subQ0]});Q15=makeQuery(id+"F0.imprint","IMPRINT",FACE,{"disambiguationData":[TD([[makeQuery(id+"F0.imprint","IMPRINT",EDGE,{"disambiguationData":[TD([[subQ2,-1.0]])],"derivedFrom":subQ1}),-1.0]])]});}
            extrude(context, id + "F3", {"entities" : qUnion([Q0, Q1, Q2, Q3, Q4, Q5, Q6, Q7, Q8, Q9, Q10, Q11, Q12, Q13, Q14, Q15]), "depth" : 20.64 * mm});
        }
        {
            var Q0;
            {var subQ0=sQuery(id+"F0.wireOp",EDGE,"E0.left");Q0=makeQuery(id+"F2.opExtrude","SWEPT_FACE",FACE,{"disambiguationData":[OSD([subQ0]),TDD([makeQuery(id+"F0.imprint","IMPRINT",EDGE,{"disambiguationData":[TD([[makeQuery(id+"F0.imprint","INTERSECT",VERTEX,{"derivedFrom":[sQuery(id+"F0.wireOp",EDGE,"E0.bottom"),subQ0]}),-1.0]])],"derivedFrom":subQ0})])]});}
            cPlane(context, id + "F4", {"entities" : qUnion([Q0]), "cplaneType" : CPlaneType.OFFSET, "offset" : 406.4 * mm, "oppositeDirection" : true, "width" : 152.4 * mm, "height" : 152.4 * mm});
        }
        {
            var Q0;
            Q0=qCreatedBy(id+"F4.planeOp",FACE);
            var sketch = newSketch(context, id + "F5", { "sketchPlane" : qUnion([Q0])});
            skLineSegment(sketch, "E29", {"start": v(0, 0) * mm, "end": v(51.4, 0) * mm});
            skLineSegment(sketch, "E30", {"start": v(20.64, -172.85) * mm, "end": v(0, -172.85) * mm});
            skLineSegment(sketch, "E31", {"start": v(20.64, -172.85) * mm, "end": v(20.64, 182.83) * mm});
            skPoint(sketch, "E32", {"position": v(20.64, -147.45) * mm});
            skPoint(sketch, "E33", {"position": v(20.64, 157.35) * mm});
            skArc(sketch, "E34", {"start": v(20.64, -147.45) * mm, "mid": v(71.44, 4.95) * mm, "end": v(20.64, 157.35) * mm});
            skArc(sketch, "E35.0", {"start": v(20.64, -125.18) * mm, "mid": v(58.74, 4.95) * mm, "end": v(20.64, 135.09) * mm});
            skSolve(sketch);
        }
        {
            var Q0;
            {var subQ0=sQuery(id+"F5.wireOp",EDGE,"E34");Q0=makeQuery(id+"F5.imprint","IMPRINT",FACE,{"disambiguationData":[TD([[makeQuery(id+"F5.imprint","IMPRINT",EDGE,{"derivedFrom":subQ0}),1.0]])]});}
            extrude(context, id + "F6", {"entities" : qUnion([Q0]), "operationType" : NewBodyOperationType.ADD, "endBound" : BoundingType.SYMMETRIC, "depth" : 12.7 * mm});
        }
        {
            var Q0;
            {var subQ0=sQuery(id+"F0.wireOp",EDGE,"E0.left");Q0=makeQuery(id+"F2.opExtrude","SWEPT_FACE",FACE,{"disambiguationData":[OSD([subQ0]),TDD([makeQuery(id+"F0.imprint","IMPRINT",EDGE,{"disambiguationData":[TD([[makeQuery(id+"F0.imprint","INTERSECT",VERTEX,{"derivedFrom":[sQuery(id+"F0.wireOp",EDGE,"E0.bottom"),subQ0]}),-1.0]])],"derivedFrom":subQ0})])]});}
            cPlane(context, id + "F7", {"entities" : qUnion([Q0]), "cplaneType" : CPlaneType.OFFSET, "offset" : 635 * mm, "oppositeDirection" : true, "width" : 152.4 * mm, "height" : 152.4 * mm});
        }
        {
            var Q0;
            Q0=qCreatedBy(id+"F7.planeOp",FACE);
            var sketch = newSketch(context, id + "F8", { "sketchPlane" : qUnion([Q0])});
            skLineSegment(sketch, "E36", {"start": v(0, -172.85) * mm, "end": v(20.64, -172.85) * mm});
            skLineSegment(sketch, "E37", {"start": v(20.64, -172.85) * mm, "end": v(20.64, 177.23) * mm});
            skPoint(sketch, "E38", {"position": v(20.64, -147.45) * mm});
            skPoint(sketch, "E39", {"position": v(20.64, 157.35) * mm});
            skArc(sketch, "E40", {"start": v(20.64, -147.45) * mm, "mid": v(71.44, 4.95) * mm, "end": v(20.64, 157.35) * mm});
            skArc(sketch, "E41.0", {"start": v(20.64, -125.18) * mm, "mid": v(58.74, 4.95) * mm, "end": v(20.64, 135.09) * mm});
            skSolve(sketch);
        }
        {
            var Q0;
            {var subQ0=sQuery(id+"F8.wireOp",EDGE,"E40");Q0=makeQuery(id+"F8.imprint","IMPRINT",FACE,{"disambiguationData":[TD([[makeQuery(id+"F8.imprint","IMPRINT",EDGE,{"derivedFrom":subQ0}),1.0]])]});}
            extrude(context, id + "F9", {"entities" : qUnion([Q0]), "operationType" : NewBodyOperationType.ADD, "endBound" : BoundingType.SYMMETRIC, "depth" : 12.7 * mm});
        }
        {
            var Q0;
            Q0=makeQuery(id+"F6.opExtrude","CAP_EDGE",EDGE,{"disambiguationData":[OSD([sQuery(id+"F5.wireOp",EDGE,"E34")])],"isStart":true});
            var Q1;
            Q1=makeQuery(id+"F6.opExtrude","CAP_EDGE",EDGE,{"disambiguationData":[OSD([sQuery(id+"F5.wireOp",EDGE,"E34")])],"isStart":false});
            var Q2;
            Q2=makeQuery(id+"F6.opExtrude","CAP_EDGE",EDGE,{"disambiguationData":[OSD([sQuery(id+"F5.wireOp",EDGE,"E35.0")])],"isStart":true});
            var Q3;
            Q3=makeQuery(id+"F6.opExtrude","CAP_EDGE",EDGE,{"disambiguationData":[OSD([sQuery(id+"F5.wireOp",EDGE,"E35.0")])],"isStart":false});
            var Q4;
            Q4=makeQuery(id+"F9.opExtrude","CAP_EDGE",EDGE,{"disambiguationData":[OSD([sQuery(id+"F8.wireOp",EDGE,"E40")])],"isStart":false});
            var Q5;
            Q5=makeQuery(id+"F9.opExtrude","CAP_EDGE",EDGE,{"disambiguationData":[OSD([sQuery(id+"F8.wireOp",EDGE,"E41.0")])],"isStart":false});
            var Q6;
            Q6=makeQuery(id+"F9.opExtrude","CAP_EDGE",EDGE,{"disambiguationData":[OSD([sQuery(id+"F8.wireOp",EDGE,"E40")])],"isStart":true});
            var Q7;
            Q7=makeQuery(id+"F9.opExtrude","CAP_EDGE",EDGE,{"disambiguationData":[OSD([sQuery(id+"F8.wireOp",EDGE,"E41.0")])],"isStart":true});
            fillet(context, id + "F10", {"entities" : qUnion([Q0, Q1, Q2, Q3, Q4, Q5, Q6, Q7]), "radius" : 6.35 * mm, "tangentPropagation" : true, "allowEdgeOverflow" : false});
        }
    });
